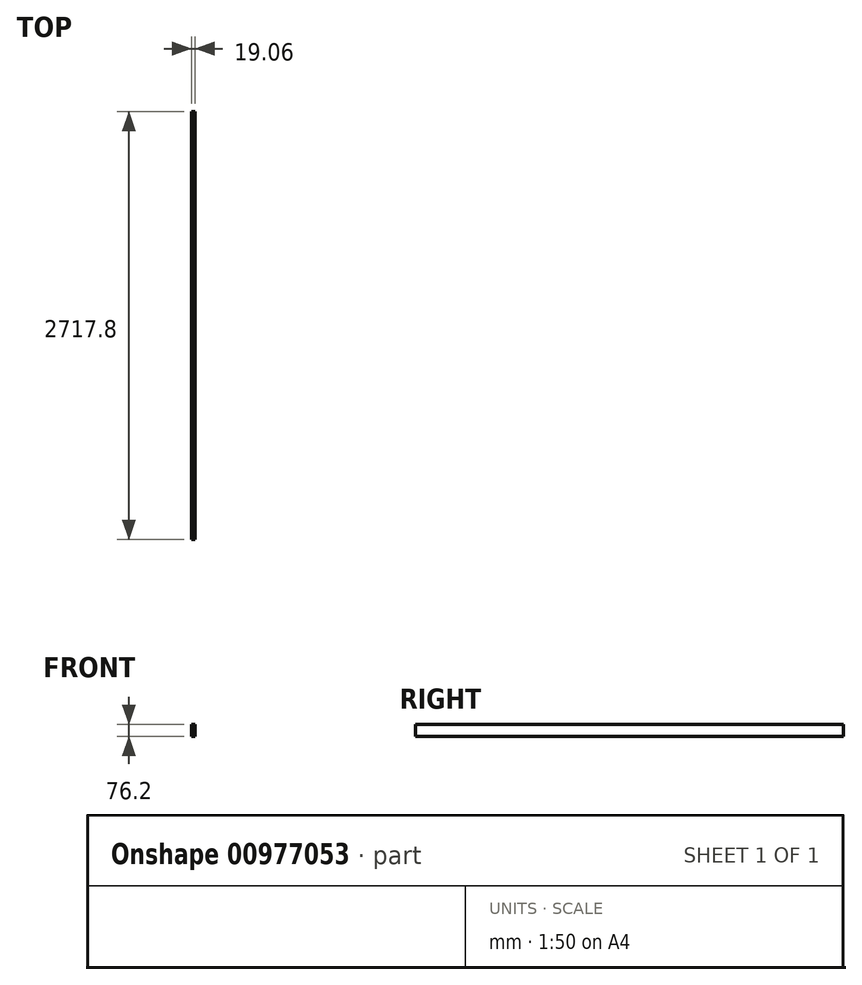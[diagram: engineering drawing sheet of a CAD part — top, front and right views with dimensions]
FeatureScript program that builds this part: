
annotation { "Feature Type Name" : "Feature", "Feature Type Description" : "" }
export const myFeature = defineFeature(function(context is Context, id is Id, definition is map)
    precondition{}
    {
        {
            var Q0;
            Q0=qCreatedBy(makeId("Front.planeOp"),FACE);
            var sketch = newSketch(context, id + "F0", { "sketchPlane" : qUnion([Q0])});
            skLineSegment(sketch, "E0.bottom", {"start": v(9.53, -38.1) * mm, "end": v(-9.52, -38.1) * mm});
            skLineSegment(sketch, "E0.top", {"start": v(9.52, 38.1) * mm, "end": v(-9.53, 38.1) * mm});
            skLineSegment(sketch, "E0.left", {"start": v(9.53, -38.1) * mm, "end": v(9.52, 38.1) * mm});
            skLineSegment(sketch, "E0.right", {"start": v(-9.52, -38.1) * mm, "end": v(-9.53, 38.1) * mm});
            skPoint(sketch, "E0.middle", {"position": v(0, 0) * mm});
            skSolve(sketch);
        }
        {
            var Q0;
            Q0 = qSketchRegion(id + "F0", true);
            extrude(context, id + "F1", {"entities" : qUnion([Q0]), "endBound" : BoundingType.SYMMETRIC, "depth" : 2717.8 * mm, "offsetDistance" : 25.4 * mm});
        }
    });
